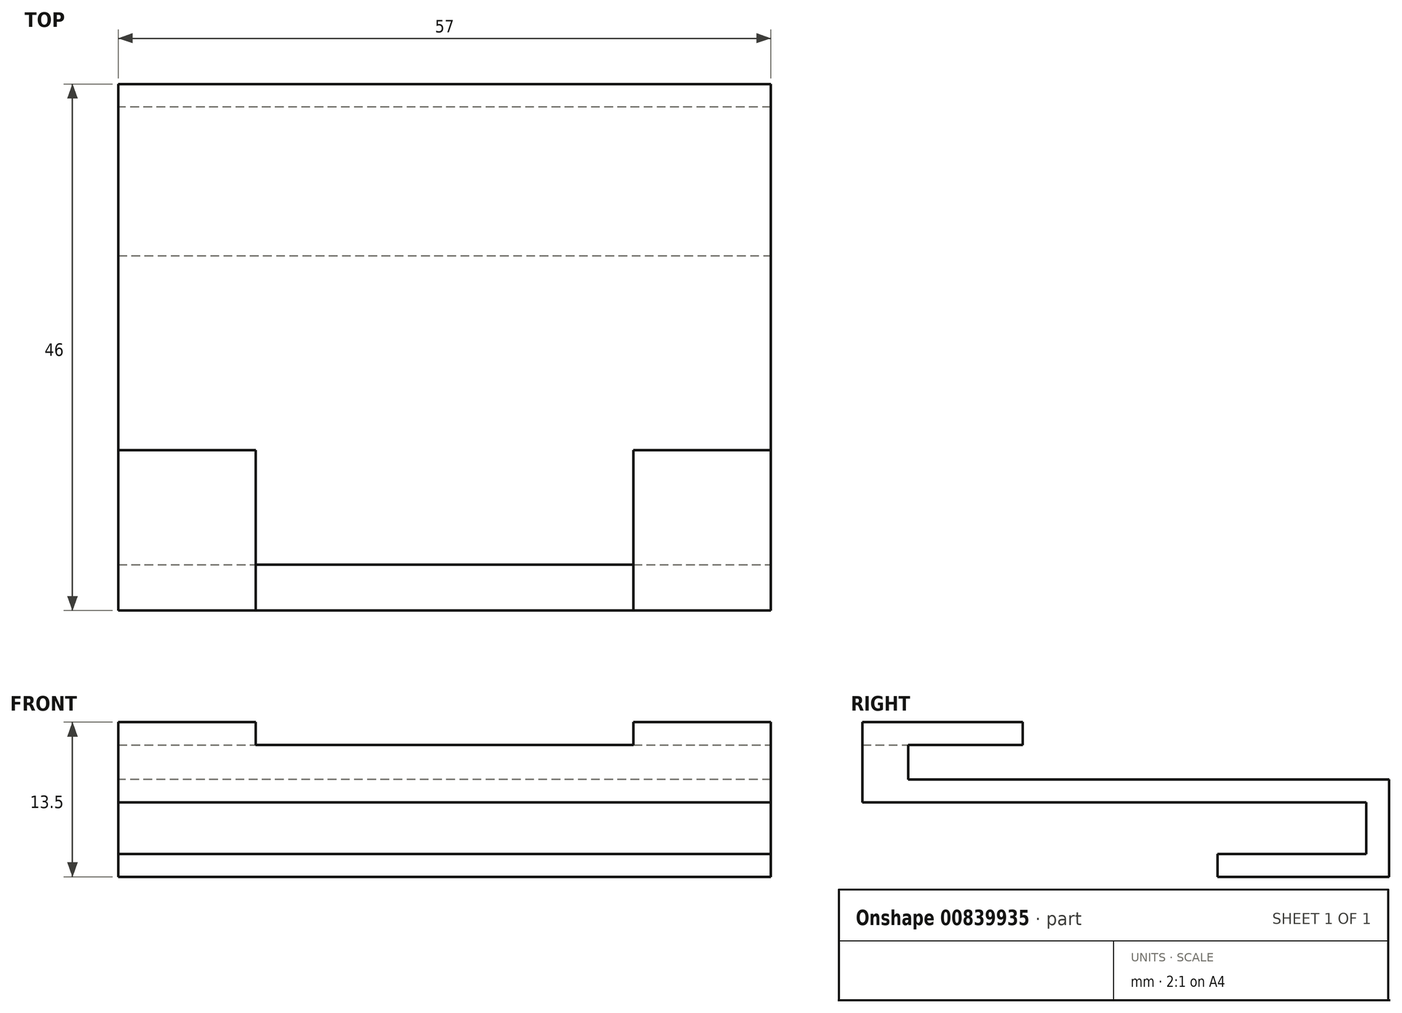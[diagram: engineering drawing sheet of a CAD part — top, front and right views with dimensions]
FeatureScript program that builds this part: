
annotation { "Feature Type Name" : "Feature", "Feature Type Description" : "" }
export const myFeature = defineFeature(function(context is Context, id is Id, definition is map)
    precondition{}
    {
        {
            var Q0;
            Q0=qCreatedBy(makeId("Top.planeOp"),FACE);
            var sketch = newSketch(context, id + "F0", { "sketchPlane" : qUnion([Q0])});
            skLineSegment(sketch, "E0.bottom", {"start": v(28.5, -23) * mm, "end": v(-28.5, -23) * mm});
            skLineSegment(sketch, "E0.top", {"start": v(28.5, 23) * mm, "end": v(-28.5, 23) * mm});
            skLineSegment(sketch, "E0.left", {"start": v(28.5, -23) * mm, "end": v(28.5, 23) * mm});
            skLineSegment(sketch, "E0.right", {"start": v(-28.5, -23) * mm, "end": v(-28.5, 23) * mm});
            skPoint(sketch, "E0.middle", {"position": v(0, 0) * mm});
            skLineSegment(sketch, "E1.bottom", {"start": v(-28.5, -23) * mm, "end": v(28.5, -23) * mm});
            skLineSegment(sketch, "E1.top", {"start": v(-28.5, -19) * mm, "end": v(28.5, -19) * mm});
            skLineSegment(sketch, "E1.left", {"start": v(-28.5, -23) * mm, "end": v(-28.5, -19) * mm});
            skLineSegment(sketch, "E1.right", {"start": v(28.5, -23) * mm, "end": v(28.5, -19) * mm});
            skLineSegment(sketch, "E2.top", {"start": v(28.5, 21) * mm, "end": v(-28.5, 21) * mm});
            skLineSegment(sketch, "E2.left", {"start": v(28.5, 23) * mm, "end": v(28.5, 21) * mm});
            skLineSegment(sketch, "E2.right", {"start": v(-28.5, 23) * mm, "end": v(-28.5, 21) * mm});
            skSolve(sketch);
        }
        {
            var Q0;
            {var subQ0=sQuery(id+"F0.wireOp",EDGE,"E1.top");var subQ8=makeQuery(id+"F0.imprint","IMPRINT",EDGE,{"derivedFrom":subQ0});var subQ10=sQuery(id+"F0.wireOp",EDGE,"E0.top");var subQ11=sQuery(id+"F0.wireOp",EDGE,"E0.bottom");Q0=qUnion([makeQuery(id+"F0.imprint","IMPRINT",FACE,{"disambiguationData":[TD([[makeQuery(id+"F0.imprint","IMPRINT",EDGE,{"derivedFrom":subQ11}),-1.0]])]}),makeQuery(id+"F0.imprint","IMPRINT",FACE,{"disambiguationData":[TD([[makeQuery(id+"F0.imprint","IMPRINT",EDGE,{"derivedFrom":subQ10}),1.0]])]}),makeQuery(id+"F0.imprint","IMPRINT",FACE,{"disambiguationData":[TD([[subQ8,1.0]])]})]);}
            extrude(context, id + "F1", {"entities" : qUnion([Q0]), "oppositeDirection" : true, "depth" : 2 * mm, "offsetDistance" : 25 * mm});
        }
        {
            var Q0;
            {var subQ0=sQuery(id+"F0.wireOp",EDGE,"E0.bottom");Q0=makeQuery(id+"F0.imprint","IMPRINT",FACE,{"disambiguationData":[TD([[makeQuery(id+"F0.imprint","IMPRINT",EDGE,{"derivedFrom":subQ0}),-1.0]])]});}
            extrude(context, id + "F2", {"entities" : qUnion([Q0]), "operationType" : NewBodyOperationType.ADD, "depth" : 3 * mm, "offsetDistance" : 25 * mm});
        }
        {
            var Q0;
            Q0=makeQuery(id+"F2.opExtrude","CAP_FACE",FACE,{"disambiguationData":[OSD([sQuery(id+"F0.wireOp",EDGE,"E0.bottom"),sQuery(id+"F0.wireOp",EDGE,"E0.left"),sQuery(id+"F0.wireOp",EDGE,"E0.right"),sQuery(id+"F0.wireOp",EDGE,"E1.top")])],"isStart":false});
            var sketch = newSketch(context, id + "F3", { "sketchPlane" : qUnion([Q0])});
            skLineSegment(sketch, "E3.bottom", {"start": v(-28.5, -23) * mm, "end": v(-16.5, -23) * mm});
            skLineSegment(sketch, "E3.top", {"start": v(-28.5, -9) * mm, "end": v(-16.5, -9) * mm});
            skLineSegment(sketch, "E3.left", {"start": v(-28.5, -23) * mm, "end": v(-28.5, -9) * mm});
            skLineSegment(sketch, "E3.right", {"start": v(-16.5, -23) * mm, "end": v(-16.5, -9) * mm});
            skLineSegment(sketch, "E4.bottom", {"start": v(28.5, -23) * mm, "end": v(16.5, -23) * mm});
            skLineSegment(sketch, "E4.top", {"start": v(28.5, -9) * mm, "end": v(16.5, -9) * mm});
            skLineSegment(sketch, "E4.left", {"start": v(28.5, -23) * mm, "end": v(28.5, -9) * mm});
            skLineSegment(sketch, "E4.right", {"start": v(16.5, -23) * mm, "end": v(16.5, -9) * mm});
            skSolve(sketch);
        }
        {
            var Q0;
            Q0 = qSketchRegion(id + "F3", true);
            extrude(context, id + "F4", {"entities" : qUnion([Q0]), "operationType" : NewBodyOperationType.ADD, "depth" : 2 * mm, "offsetDistance" : 25 * mm});
        }
        {
            var Q0;
            {var subQ0=sQuery(id+"F0.wireOp",EDGE,"E0.top");Q0=makeQuery(id+"F0.imprint","IMPRINT",FACE,{"disambiguationData":[TD([[makeQuery(id+"F0.imprint","IMPRINT",EDGE,{"derivedFrom":subQ0}),1.0]])]});}
            extrude(context, id + "F5", {"entities" : qUnion([Q0]), "operationType" : NewBodyOperationType.ADD, "oppositeDirection" : true, "depth" : 6.5 * mm, "offsetDistance" : 25 * mm});
        }
        {
            var Q0;
            Q0=makeQuery(id+"F5.opExtrude","CAP_FACE",FACE,{"disambiguationData":[OSD([sQuery(id+"F0.wireOp",EDGE,"E0.top"),sQuery(id+"F0.wireOp",EDGE,"E0.left"),sQuery(id+"F0.wireOp",EDGE,"E0.right"),sQuery(id+"F0.wireOp",EDGE,"E2.top")])],"isStart":false});
            var sketch = newSketch(context, id + "F6", { "sketchPlane" : qUnion([Q0])});
            skLineSegment(sketch, "E5.bottom", {"start": v(-28.5, -23) * mm, "end": v(28.5, -23) * mm});
            skLineSegment(sketch, "E5.top", {"start": v(-28.5, -8) * mm, "end": v(28.5, -8) * mm});
            skLineSegment(sketch, "E5.left", {"start": v(-28.5, -23) * mm, "end": v(-28.5, -8) * mm});
            skLineSegment(sketch, "E5.right", {"start": v(28.5, -23) * mm, "end": v(28.5, -8) * mm});
            skSolve(sketch);
        }
        {
            var Q0;
            {var subQ0=sQuery(id+"F6.wireOp",EDGE,"E5.top");Q0=makeQuery(id+"F6.imprint","IMPRINT",FACE,{"disambiguationData":[TD([[makeQuery(id+"F6.imprint","IMPRINT",EDGE,{"derivedFrom":subQ0}),-1.0]])]});}
            var Q1;
            {var subQ0=sQuery(id+"F6.wireOp",EDGE,"E5.bottom");Q1=makeQuery(id+"F6.imprint","IMPRINT",FACE,{"disambiguationData":[TD([[makeQuery(id+"F6.imprint","IMPRINT",EDGE,{"derivedFrom":subQ0}),-1.0]])]});}
            extrude(context, id + "F7", {"entities" : qUnion([Q0, Q1]), "operationType" : NewBodyOperationType.ADD, "depth" : 2 * mm, "offsetDistance" : 25 * mm});
        }
    });
